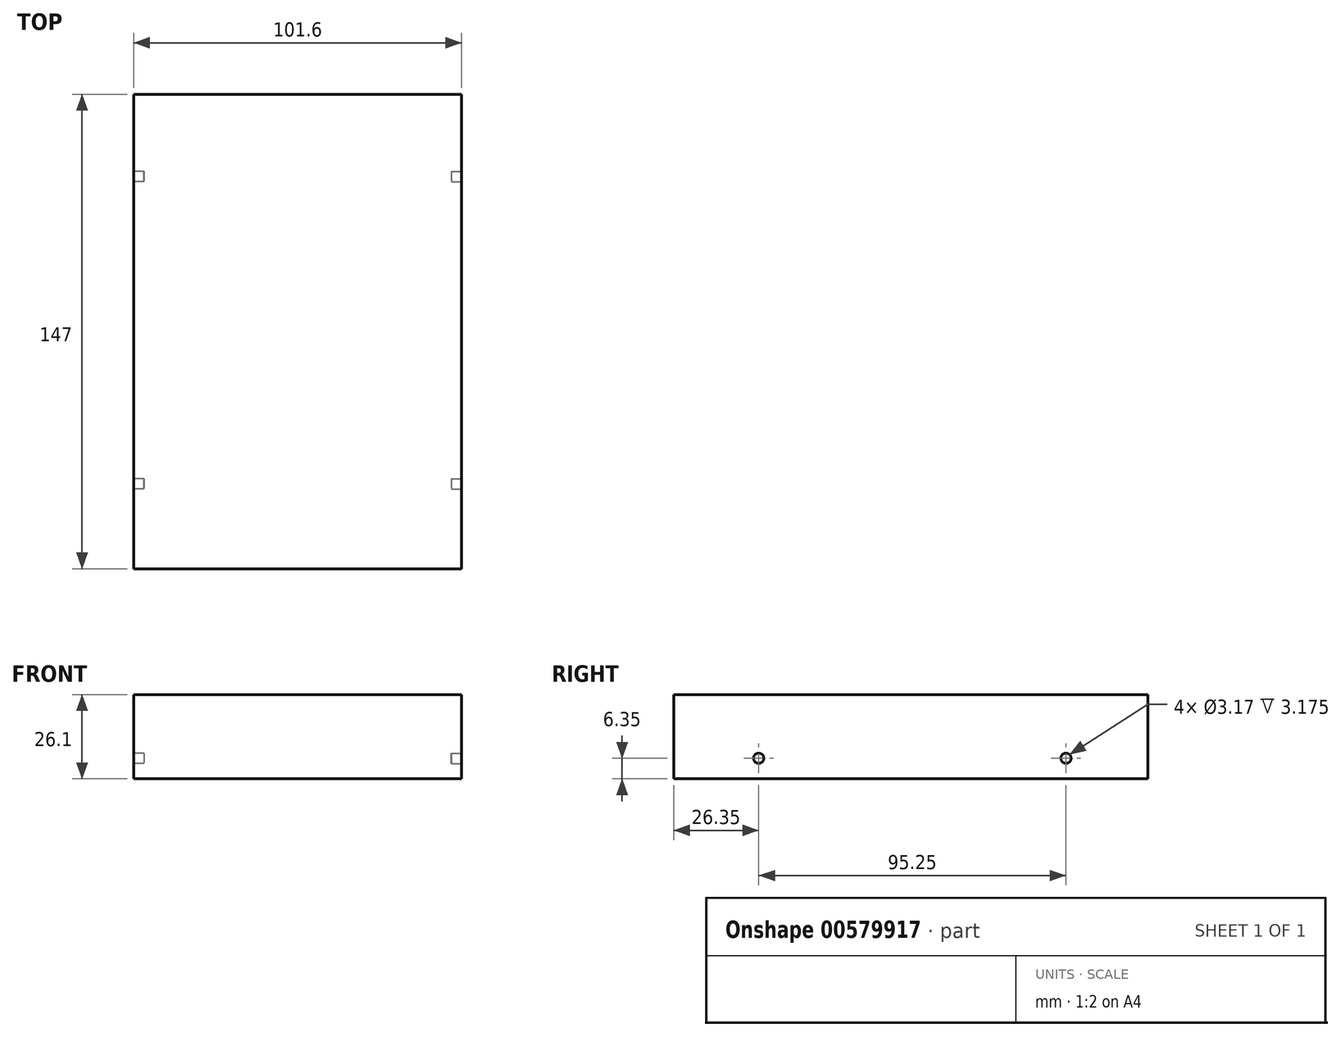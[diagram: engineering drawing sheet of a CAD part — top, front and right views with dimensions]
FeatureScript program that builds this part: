
annotation { "Feature Type Name" : "Feature", "Feature Type Description" : "" }
export const myFeature = defineFeature(function(context is Context, id is Id, definition is map)
    precondition{}
    {
        {
            var Q0;
            Q0=qCreatedBy(makeId("Top.planeOp"),FACE);
            var sketch = newSketch(context, id + "F0", { "sketchPlane" : qUnion([Q0])});
            skLineSegment(sketch, "E0.bottom", {"start": v(0, 0) * mm, "end": v(101.6, 0) * mm});
            skLineSegment(sketch, "E0.top", {"start": v(0, 147) * mm, "end": v(101.6, 147) * mm});
            skLineSegment(sketch, "E0.left", {"start": v(0, 0) * mm, "end": v(0, 147) * mm});
            skLineSegment(sketch, "E0.right", {"start": v(101.6, 0) * mm, "end": v(101.6, 147) * mm});
            skSolve(sketch);
        }
        {
            var Q0;
            Q0 = qSketchRegion(id + "F0", true);
            extrude(context, id + "F1", {"entities" : qUnion([Q0]), "depth" : 26.1 * mm, "offsetDistance" : 25.4 * mm});
        }
        {
            var Q0;
            Q0=makeQuery(id+"F1.opExtrude","SWEPT_FACE",FACE,{"disambiguationData":[OSD([sQuery(id+"F0.wireOp",EDGE,"E0.left")])]});
            var sketch = newSketch(context, id + "F2", { "sketchPlane" : qUnion([Q0])});
            skCircle(sketch, "E1", {"center": v(-121.6, 6.35) * mm, "radius": 1.59 * mm});
            skCircle(sketch, "E2", {"center": v(-26.35, 6.35) * mm, "radius": 1.59 * mm});
            skSolve(sketch);
        }
        {
            var Q0;
            Q0 = qSketchRegion(id + "F2", true);
            extrude(context, id + "F3", {"entities" : qUnion([Q0]), "operationType" : NewBodyOperationType.REMOVE, "oppositeDirection" : true, "depth" : 3.17 * mm, "offsetDistance" : 25.4 * mm});
        }
        {
            var Q0;
            Q0=makeQuery(id+"F1.opExtrude","SWEPT_FACE",FACE,{"disambiguationData":[OSD([sQuery(id+"F0.wireOp",EDGE,"E0.right")])]});
            var sketch = newSketch(context, id + "F4", { "sketchPlane" : qUnion([Q0])});
            skCircle(sketch, "E3", {"center": v(26.35, 6.35) * mm, "radius": 1.59 * mm});
            skCircle(sketch, "E4", {"center": v(121.6, 6.35) * mm, "radius": 1.59 * mm});
            skSolve(sketch);
        }
        {
            var Q0;
            Q0 = qSketchRegion(id + "F4", true);
            extrude(context, id + "F5", {"entities" : qUnion([Q0]), "operationType" : NewBodyOperationType.REMOVE, "oppositeDirection" : true, "depth" : 3.17 * mm, "offsetDistance" : 25.4 * mm});
        }
    });
